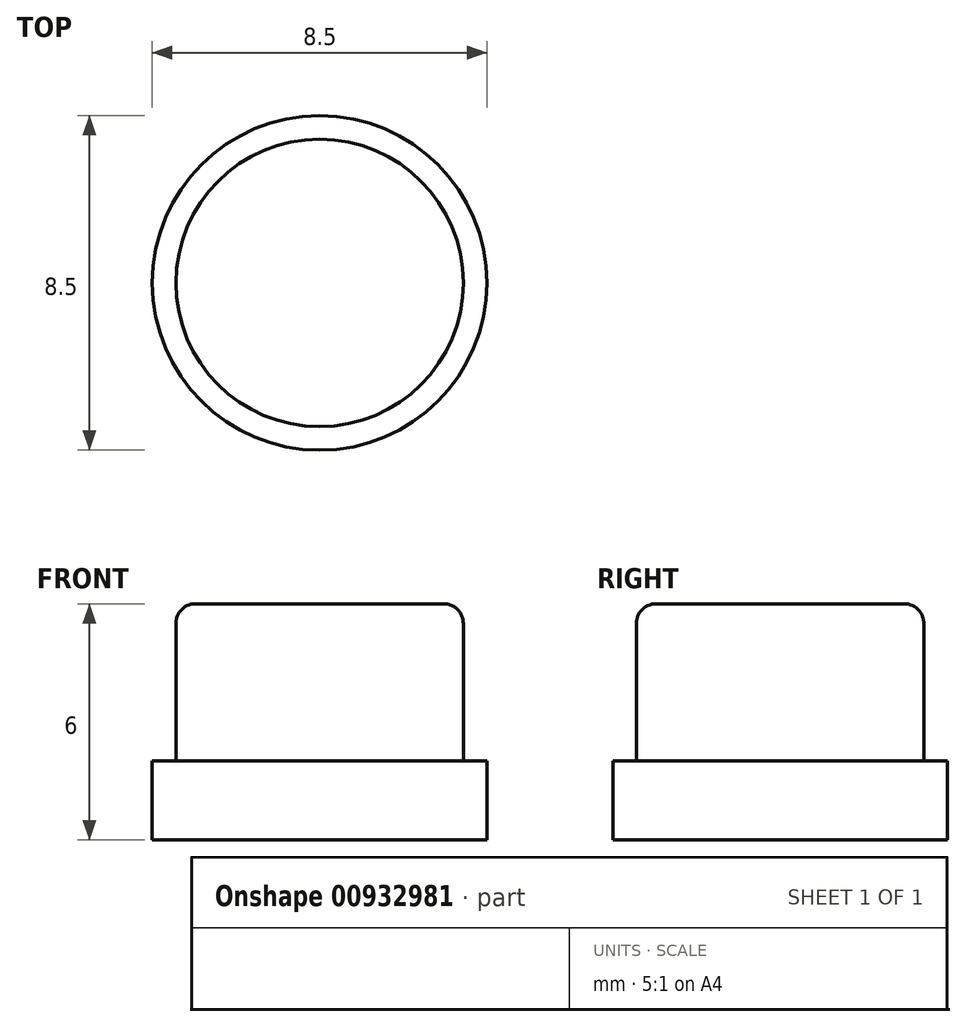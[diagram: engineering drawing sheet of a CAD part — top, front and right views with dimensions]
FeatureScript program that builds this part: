
annotation { "Feature Type Name" : "Feature", "Feature Type Description" : "" }
export const myFeature = defineFeature(function(context is Context, id is Id, definition is map)
    precondition{}
    {
        {
            var Q0;
            Q0=qCreatedBy(makeId("Top.planeOp"),FACE);
            var sketch = newSketch(context, id + "F0", { "sketchPlane" : qUnion([Q0])});
            skCircle(sketch, "E0", {"center": v(0, 0) * mm, "radius": 3.65 * mm});
            skCircle(sketch, "E1", {"center": v(0, 0) * mm, "radius": 4.25 * mm});
            skText(sketch, "E2", { "text": "Up", "fontName": "OpenSans-Bold.ttf"});
            const initialGuessF0  = {"E2": [-0.00318, -0.0016, 1, 0, 0.00324]};
            skSetInitialGuess(sketch, initialGuessF0);
            skSolve(sketch);
        }
        {
            var Q0;
            Q0=makeQuery(id+"F0.imprint","IMPRINT",FACE,{"disambiguationData":[TD([[makeQuery(id+"F0.imprint","IMPRINT",EDGE,{"derivedFrom":sQuery(id+"F0.wireOp",EDGE,"E0")}),1.0]])]});
            var Q1;
            Q1=makeQuery(id+"F0.imprint","IMPRINT",FACE,{"disambiguationData":[TD([[makeQuery(id+"F0.imprint","IMPRINT",EDGE,{"derivedFrom":sQuery(id+"F0.wireOp",EDGE,"E2.sketch_text.stroke-0")}),-1.0]])]});
            var Q2;
            Q2=makeQuery(id+"F0.imprint","IMPRINT",FACE,{"disambiguationData":[TD([[makeQuery(id+"F0.imprint","IMPRINT",EDGE,{"derivedFrom":sQuery(id+"F0.wireOp",EDGE,"E2.sketch_text.stroke-15")}),-1.0]])]});
            var Q3;
            Q3=makeQuery(id+"F0.imprint","IMPRINT",FACE,{"disambiguationData":[TD([[makeQuery(id+"F0.imprint","IMPRINT",EDGE,{"derivedFrom":sQuery(id+"F0.wireOp",EDGE,"E2.sketch_text.stroke-30")}),1.0]])]});
            extrude(context, id + "F1", {"entities" : qUnion([Q0, Q1, Q2, Q3]), "depth" : 6 * mm, "offsetDistance" : 25 * mm});
        }
        {
            var Q0;
            Q0=makeQuery(id+"F0.imprint","IMPRINT",FACE,{"disambiguationData":[TD([[makeQuery(id+"F0.imprint","IMPRINT",EDGE,{"derivedFrom":sQuery(id+"F0.wireOp",EDGE,"E0")}),-1.0]])]});
            extrude(context, id + "F2", {"entities" : qUnion([Q0]), "operationType" : NewBodyOperationType.ADD, "depth" : 2 * mm, "offsetDistance" : 25 * mm});
        }
        {
            var Q0;
            Q0=makeQuery(id+"F1.opExtrude","CAP_EDGE",EDGE,{"disambiguationData":[OSD([sQuery(id+"F0.wireOp",EDGE,"E0")])],"isStart":false});
            fillet(context, id + "F3", {"entities" : qUnion([Q0]), "radius" : .5 * mm, "tangentPropagation" : true, "allowEdgeOverflow" : false});
        }
    });
